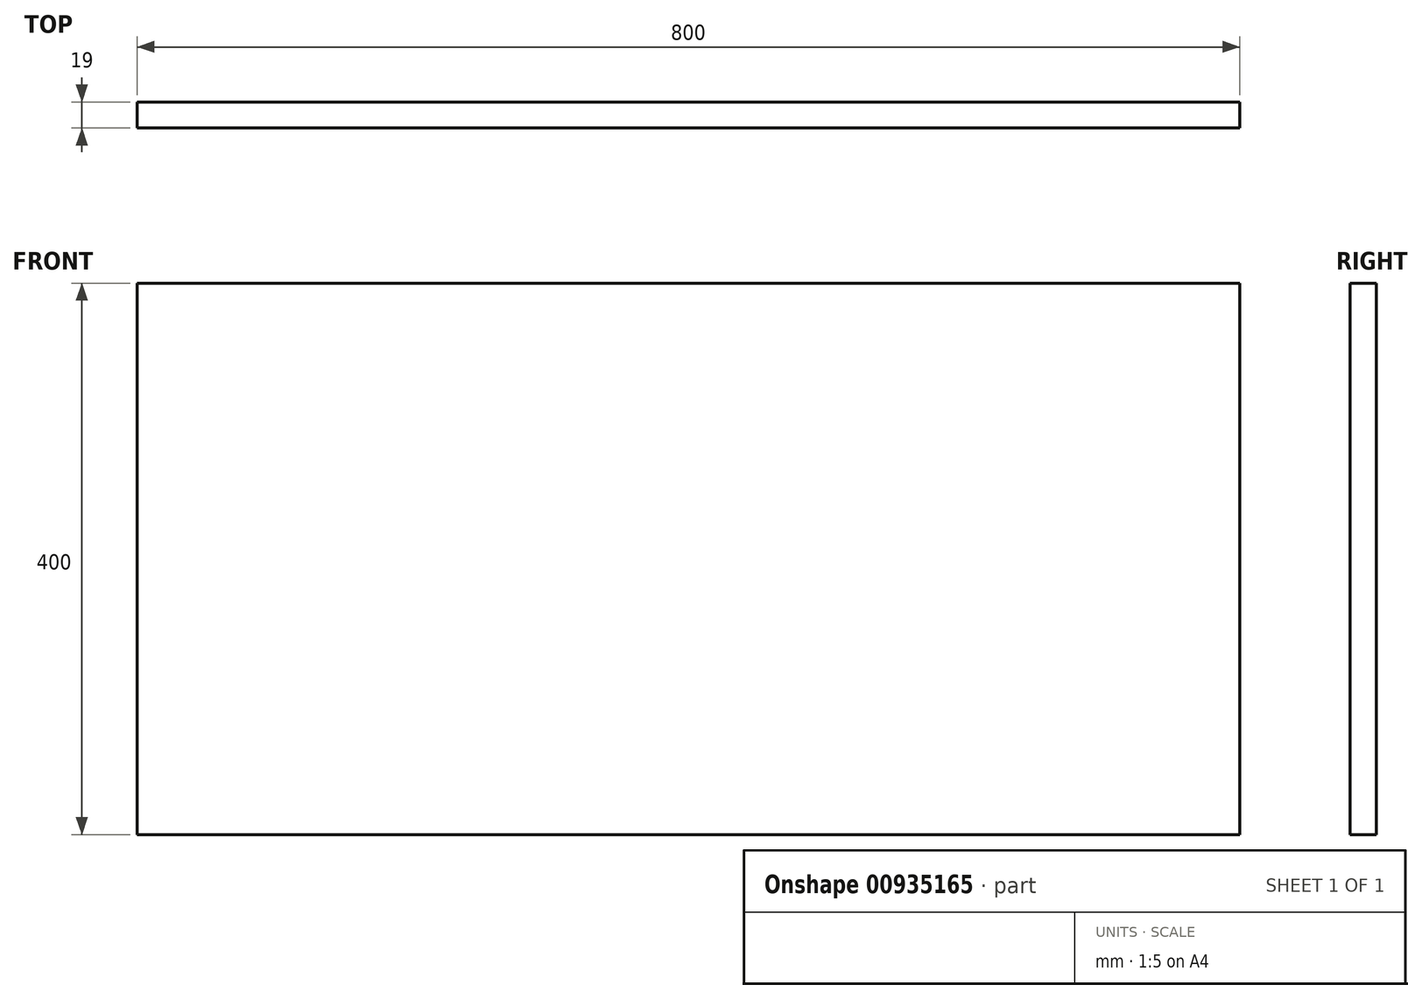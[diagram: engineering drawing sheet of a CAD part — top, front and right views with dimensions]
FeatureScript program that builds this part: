
annotation { "Feature Type Name" : "Feature", "Feature Type Description" : "" }
export const myFeature = defineFeature(function(context is Context, id is Id, definition is map)
    precondition{}
    {
        {
            var Q0;
            Q0=qCreatedBy(makeId("Front.planeOp"),FACE);
            var sketch = newSketch(context, id + "F0", { "sketchPlane" : qUnion([Q0])});
            skLineSegment(sketch, "E0.bottom", {"start": v(0, 0) * mm, "end": v(800, 0) * mm});
            skLineSegment(sketch, "E0.top", {"start": v(0, 400) * mm, "end": v(800, 400) * mm});
            skLineSegment(sketch, "E0.left", {"start": v(0, 0) * mm, "end": v(0, 400) * mm});
            skLineSegment(sketch, "E0.right", {"start": v(800, 0) * mm, "end": v(800, 400) * mm});
            skSolve(sketch);
        }
        {
            var Q0;
            Q0 = qSketchRegion(id + "F0", true);
            extrude(context, id + "F1", {"entities" : qUnion([Q0]), "depth" : 19 * mm, "offsetDistance" : 25 * mm});
        }
    });
